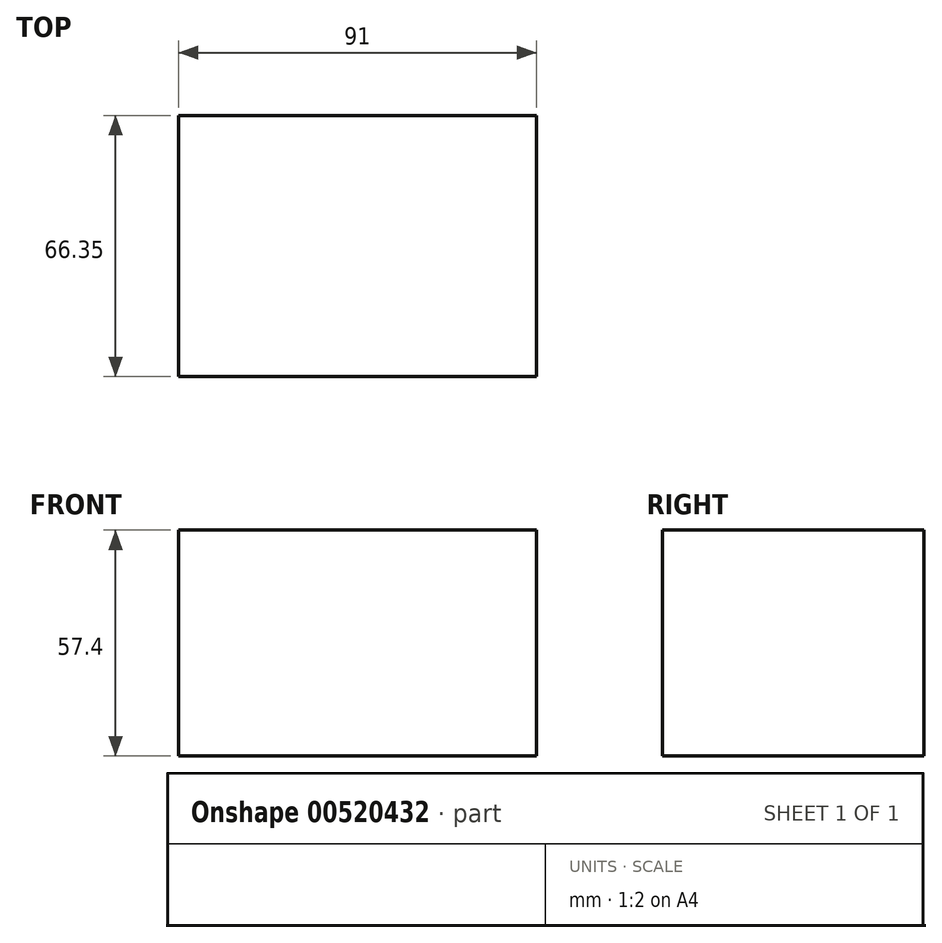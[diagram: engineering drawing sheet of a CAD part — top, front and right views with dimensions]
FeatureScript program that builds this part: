
annotation { "Feature Type Name" : "Feature", "Feature Type Description" : "" }
export const myFeature = defineFeature(function(context is Context, id is Id, definition is map)
    precondition{}
    {
        {
            var Q0;
            Q0=qCreatedBy(makeId("Top.planeOp"),FACE);
            var sketch = newSketch(context, id + "F0", { "sketchPlane" : qUnion([Q0])});
            skLineSegment(sketch, "E0.bottom", {"start": v(-55.19, -38.14) * mm, "end": v(35.81, -38.14) * mm});
            skLineSegment(sketch, "E0.top", {"start": v(-55.19, 28.2) * mm, "end": v(35.81, 28.2) * mm});
            skLineSegment(sketch, "E0.left", {"start": v(-55.19, -38.14) * mm, "end": v(-55.19, 28.2) * mm});
            skLineSegment(sketch, "E0.right", {"start": v(35.81, -38.14) * mm, "end": v(35.81, 28.2) * mm});
            skSolve(sketch);
        }
        {
            var Q0;
            Q0 = qSketchRegion(id + "F0", true);
            extrude(context, id + "F1", {"entities" : qUnion([Q0]), "depth" : 57.4 * mm, "offsetDistance" : 25.4 * mm});
        }
        {
            var Q0;
            Q0=makeQuery(id+"F1.opExtrude","CAP_FACE",FACE,{"disambiguationData":[OSD([sQuery(id+"F0.wireOp",EDGE,"E0.bottom"),sQuery(id+"F0.wireOp",EDGE,"E0.top"),sQuery(id+"F0.wireOp",EDGE,"E0.left"),sQuery(id+"F0.wireOp",EDGE,"E0.right")])],"isStart":false});
            var sketch = newSketch(context, id + "F2", { "sketchPlane" : qUnion([Q0])});
            skSolve(sketch);
        }
        {
            var Q0;
            Q0=makeQuery(id+"F2.imprint","IMPRINT",FACE,{"disambiguationData":[TD([[makeQuery(id+"F2.imprint","IMPRINT",EDGE,{"derivedFrom":makeQuery(id+"F1.opExtrude","CAP_EDGE",EDGE,{"disambiguationData":[OSD([sQuery(id+"F0.wireOp",EDGE,"E0.bottom")])],"isStart":false})}),1.0]])]});
            var sketch = newSketch(context, id + "F3", { "sketchPlane" : qUnion([Q0])});
            skCircle(sketch, "E1", {"center": v(-10.14, 0) * mm, "radius": 20.26 * mm});
            skSolve(sketch);
        }
        {
            var Q0;
            Q0=sQuery(id+"F3.wireOp",EDGE,"E1");
            extrude(context, id + "F4", {"bodyType" : ToolBodyType.SURFACE, "surfaceEntities" : qUnion([Q0]), "depth" : 33.78 * mm, "offsetDistance" : 25.4 * mm});
        }
    });
